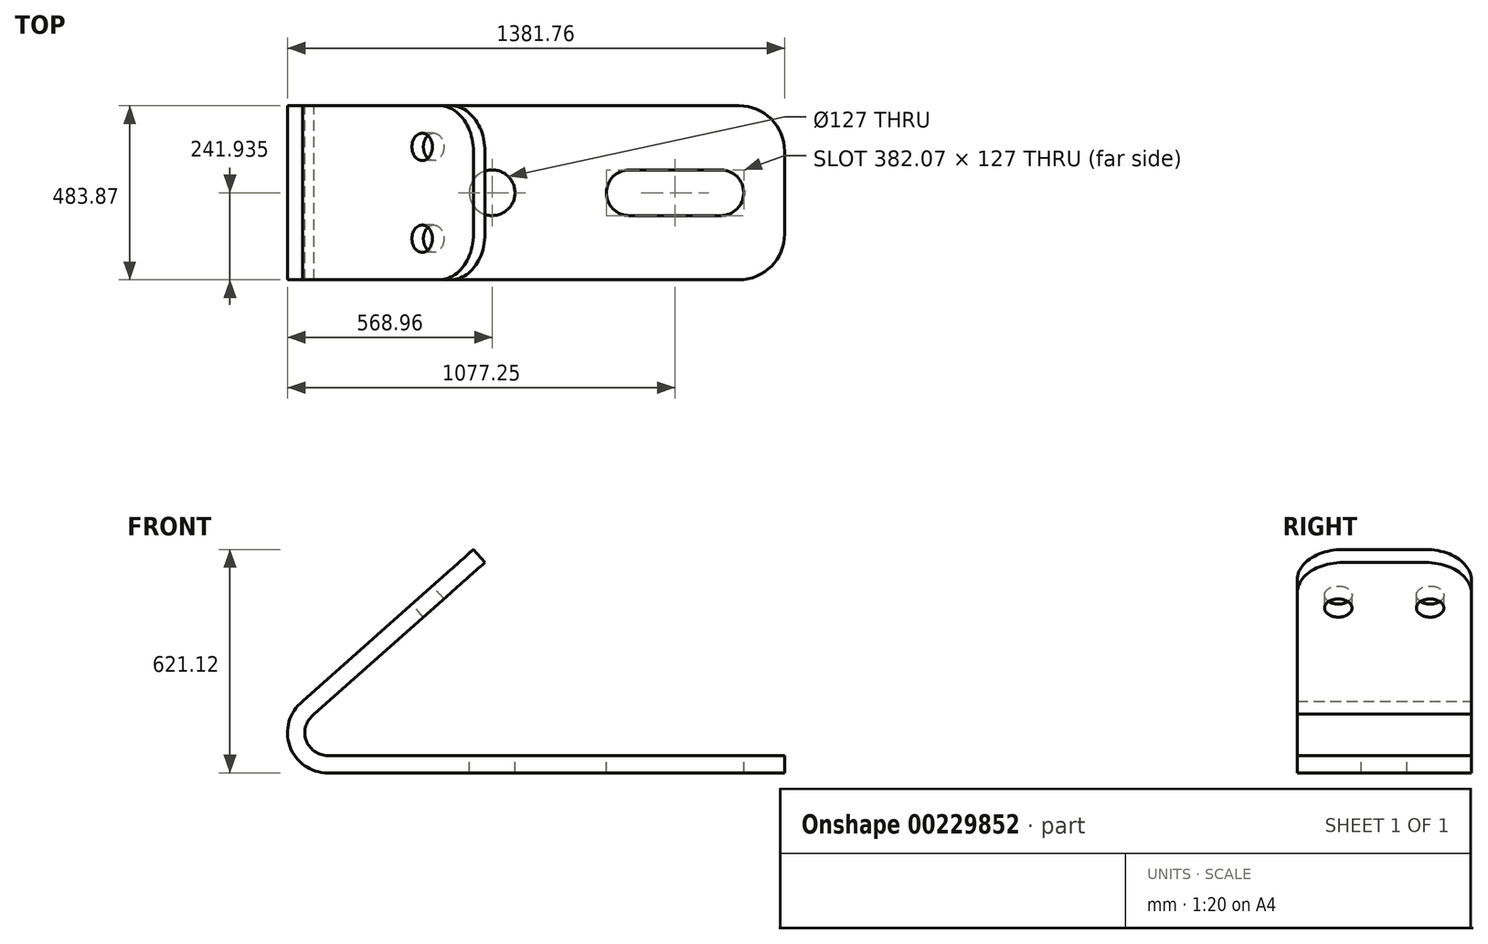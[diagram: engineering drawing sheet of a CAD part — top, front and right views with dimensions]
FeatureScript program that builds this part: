
annotation { "Feature Type Name" : "Feature", "Feature Type Description" : "" }
export const myFeature = defineFeature(function(context is Context, id is Id, definition is map)
    precondition{}
    {
        {
            var Q0;
            Q0=qCreatedBy(makeId("Front.planeOp"),FACE);
            var sketch = newSketch(context, id + "F0", { "sketchPlane" : qUnion([Q0])});
            skLineSegment(sketch, "E0.bottom", {"start": v(-363.41, 23.9) * mm, "end": v(906.59, 23.9) * mm});
            skLineSegment(sketch, "E0.top", {"start": v(-363.41, -24.37) * mm, "end": v(906.59, -24.37) * mm});
            skLineSegment(sketch, "E0.left", {"start": v(-363.41, 23.9) * mm, "end": v(-363.41, -24.37) * mm});
            skLineSegment(sketch, "E0.right", {"start": v(906.59, 23.9) * mm, "end": v(906.59, -24.37) * mm});
            skArc(sketch, "E1", {"start": v(-363.41, 199.15) * mm, "mid": v(-475.17, 87.4) * mm, "end": v(-363.41, -24.37) * mm});
            skLineSegment(sketch, "E2", {"start": v(-433.04, 174.81) * mm, "end": v(41.5, 596.75) * mm});
            skLineSegment(sketch, "E3", {"start": v(41.5, 596.75) * mm, "end": v(73.58, 560.68) * mm});
            skLineSegment(sketch, "E4", {"start": v(73.58, 560.68) * mm, "end": v(-400.97, 138.75) * mm});
            skLineSegment(sketch, "E5", {"start": v(-433.04, 174.81) * mm, "end": v(-400.97, 138.75) * mm});
            skArc(sketch, "E6", {"start": v(-400.97, 138.75) * mm, "mid": v(-423.83, 67.7) * mm, "end": v(-363.41, 23.9) * mm});
            skSolve(sketch);
        }
        {
            var Q0;
            Q0 = qSketchRegion(id + "F0", true);
            extrude(context, id + "F1", {"entities" : qUnion([Q0]), "depth" : 483.87 * mm});
        }
        {
            var Q0;
            Q0=makeQuery(id+"F1.opExtrude","CAP_EDGE",EDGE,{"disambiguationData":[OSD([sQuery(id+"F0.wireOp",EDGE,"E3")])],"isStart":true});
            var Q1;
            Q1=makeQuery(id+"F1.opExtrude","CAP_EDGE",EDGE,{"disambiguationData":[OSD([sQuery(id+"F0.wireOp",EDGE,"E3")])],"isStart":false});
            fillet(context, id + "F2", {"entities" : qUnion([Q0, Q1]), "radius" : 127 * mm, "tangentPropagation" : true, "allowEdgeOverflow" : false});
        }
        {
            var Q0;
            Q0=makeQuery(id+"F1.opExtrude","CAP_EDGE",EDGE,{"disambiguationData":[OSD([sQuery(id+"F0.wireOp",EDGE,"E0.right")])],"isStart":false});
            var Q1;
            Q1=makeQuery(id+"F1.opExtrude","CAP_EDGE",EDGE,{"disambiguationData":[OSD([sQuery(id+"F0.wireOp",EDGE,"E0.right")])],"isStart":true});
            fillet(context, id + "F3", {"entities" : qUnion([Q0, Q1]), "radius" : 127 * mm, "tangentPropagation" : true, "allowEdgeOverflow" : false});
        }
        {
            var Q0;
            Q0=makeQuery(id+"F1.opExtrude","SWEPT_FACE",FACE,{"disambiguationData":[OSD([sQuery(id+"F0.wireOp",EDGE,"E2")])]});
            var sketch = newSketch(context, id + "F4", { "sketchPlane" : qUnion([Q0])});
            skCircle(sketch, "E7", {"center": v(237.04, -114.3) * mm, "radius": 38.1 * mm});
            skCircle(sketch, "E8", {"center": v(237.04, -369.57) * mm, "radius": 38.1 * mm});
            skSolve(sketch);
        }
        {
            var Q0;
            Q0 = qSketchRegion(id + "F4", true);
            extrude(context, id + "F5", {"entities" : qUnion([Q0]), "operationType" : NewBodyOperationType.REMOVE, "oppositeDirection" : true, "depth" : 119.38 * mm});
        }
        {
            var Q0;
            Q0=makeQuery(id+"F1.opExtrude","SWEPT_FACE",FACE,{"disambiguationData":[OSD([sQuery(id+"F0.wireOp",EDGE,"E0.bottom")])]});
            var sketch = newSketch(context, id + "F6", { "sketchPlane" : qUnion([Q0])});
            skPoint(sketch, "E9.startSnap0", {"position": v(906.59, -241.94) * mm});
            skCircle(sketch, "E10", {"center": v(93.79, -241.94) * mm, "radius": 63.5 * mm});
            skCircle(sketch, "E11", {"center": v(729.61, -241.94) * mm, "radius": 63.5 * mm});
            skCircle(sketch, "E12", {"center": v(474.55, -241.94) * mm, "radius": 63.5 * mm});
            skLineSegment(sketch, "E13", {"start": v(474.55, -178.44) * mm, "end": v(729.61, -178.44) * mm});
            skLineSegment(sketch, "E14", {"start": v(474.55, -305.44) * mm, "end": v(729.61, -305.44) * mm});
            skSolve(sketch);
        }
        {
            var Q0;
            Q0=makeQuery(id+"F6.imprint","IMPRINT",FACE,{"disambiguationData":[TD([[makeQuery(id+"F6.imprint","IMPRINT",EDGE,{"derivedFrom":sQuery(id+"F6.wireOp",EDGE,"E10")}),1.0]])]});
            var Q1;
            {var subQ0=sQuery(id+"F6.wireOp",EDGE,"E12");var subQ1=makeQuery(id+"F6.imprint","INTERSECT",VERTEX,{"derivedFrom":[subQ0,sQuery(id+"F6.wireOp",EDGE,"E13")]});Q1=makeQuery(id+"F6.imprint","IMPRINT",FACE,{"disambiguationData":[TD([[makeQuery(id+"F6.imprint","IMPRINT",EDGE,{"disambiguationData":[TD([[subQ1,-1.0]])],"derivedFrom":subQ0}),1.0]])]});}
            var Q2;
            {var subQ0=sQuery(id+"F6.wireOp",EDGE,"E13");Q2=makeQuery(id+"F6.imprint","IMPRINT",FACE,{"disambiguationData":[TD([[makeQuery(id+"F6.imprint","IMPRINT",EDGE,{"derivedFrom":subQ0}),-1.0]])]});}
            var Q3;
            {var subQ0=sQuery(id+"F6.wireOp",EDGE,"E11");var subQ1=makeQuery(id+"F6.imprint","INTERSECT",VERTEX,{"derivedFrom":[subQ0,sQuery(id+"F6.wireOp",EDGE,"E13")]});Q3=makeQuery(id+"F6.imprint","IMPRINT",FACE,{"disambiguationData":[TD([[makeQuery(id+"F6.imprint","IMPRINT",EDGE,{"disambiguationData":[TD([[subQ1,-1.0]])],"derivedFrom":subQ0}),1.0]])]});}
            extrude(context, id + "F7", {"entities" : qUnion([Q0, Q1, Q2, Q3]), "operationType" : NewBodyOperationType.REMOVE, "oppositeDirection" : true, "depth" : 76.2 * mm, "hasSecondDirection" : true, "secondDirectionOppositeDirection" : false, "secondDirectionDepth" : 76.2 * mm});
        }
    });
